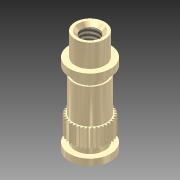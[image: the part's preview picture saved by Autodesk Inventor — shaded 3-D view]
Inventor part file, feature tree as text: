
AUTODESK INVENTOR PART (.ipt)
format: ipt  version: 2011 (Build 150239000, 239)  size: 242,176 bytes
history: native  units: in
note: dims shown in document units (in); Inventor stores cm internally (conversion verified against a paired STEP export)
features: other x1, imported_body x1, thread x1
ambient origin geometry x8: Origin, YZ Plane, XZ Plane, XY Plane, X Axis, Y Axis, Z Axis, Center Point
feature tree (3):
  parser-record x1  (decoder bookkeeping rows leaked as tree rows — omitted from the tree; the rows remain in map.json)
  imported_body  "Base1"
  thread  "Thread1"  [1 undecoded]
note: 1 required parameter value undecoded (feature->parameter linkage not recoverable at this tier; creation-order binding heuristic only, values carry confidence <= 0.55)
